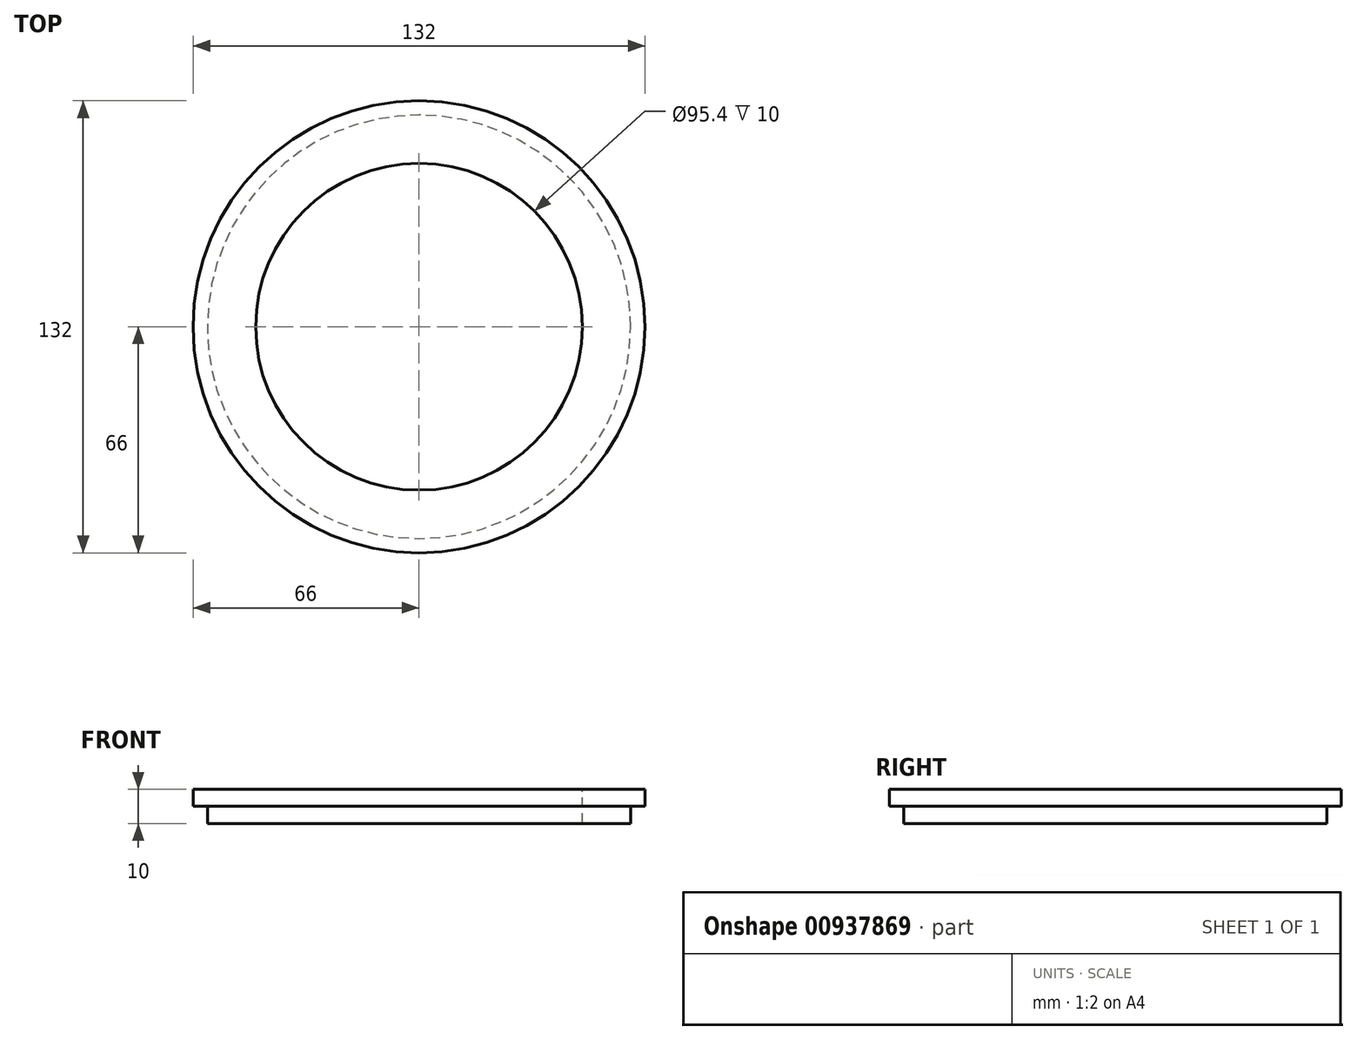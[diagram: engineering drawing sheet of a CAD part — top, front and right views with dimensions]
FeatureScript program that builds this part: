
annotation { "Feature Type Name" : "Feature", "Feature Type Description" : "" }
export const myFeature = defineFeature(function(context is Context, id is Id, definition is map)
    precondition{}
    {
        {
            var Q0;
            Q0=qCreatedBy(makeId("Front.planeOp"),FACE);
            var sketch = newSketch(context, id + "F0", { "sketchPlane" : qUnion([Q0])});
            skLineSegment(sketch, "E0", {"start": v(66, 10) * mm, "end": v(66, 5) * mm});
            skLineSegment(sketch, "E1", {"start": v(66, 10) * mm, "end": v(47.7, 10) * mm});
            skLineSegment(sketch, "E2", {"start": v(47.7, 10) * mm, "end": v(47.7, 0) * mm});
            skLineSegment(sketch, "E3", {"start": v(66, 5) * mm, "end": v(61.8, 5) * mm});
            skLineSegment(sketch, "E4", {"start": v(61.8, 5) * mm, "end": v(61.8, 0) * mm});
            skLineSegment(sketch, "E5", {"start": v(61.8, 0) * mm, "end": v(47.7, 0) * mm});
            skLineSegment(sketch, "E6", {"start": v(0, 68.92) * mm, "end": v(0, -69.3) * mm, "construction": true});
            skSolve(sketch);
        }
        {
            var Q0;
            Q0 = qSketchRegion(id + "F0", true);
            var Q1;
            Q1=sQuery(id+"F0.wireOp",EDGE,"E6");
            revolve(context, id + "F1", {"surfaceOperationType" : NewSurfaceOperationType.NEW, "entities" : qUnion([Q0]), "axis" : qUnion([Q1]), "revolveType" : RevolveType.FULL});
        }
    });
